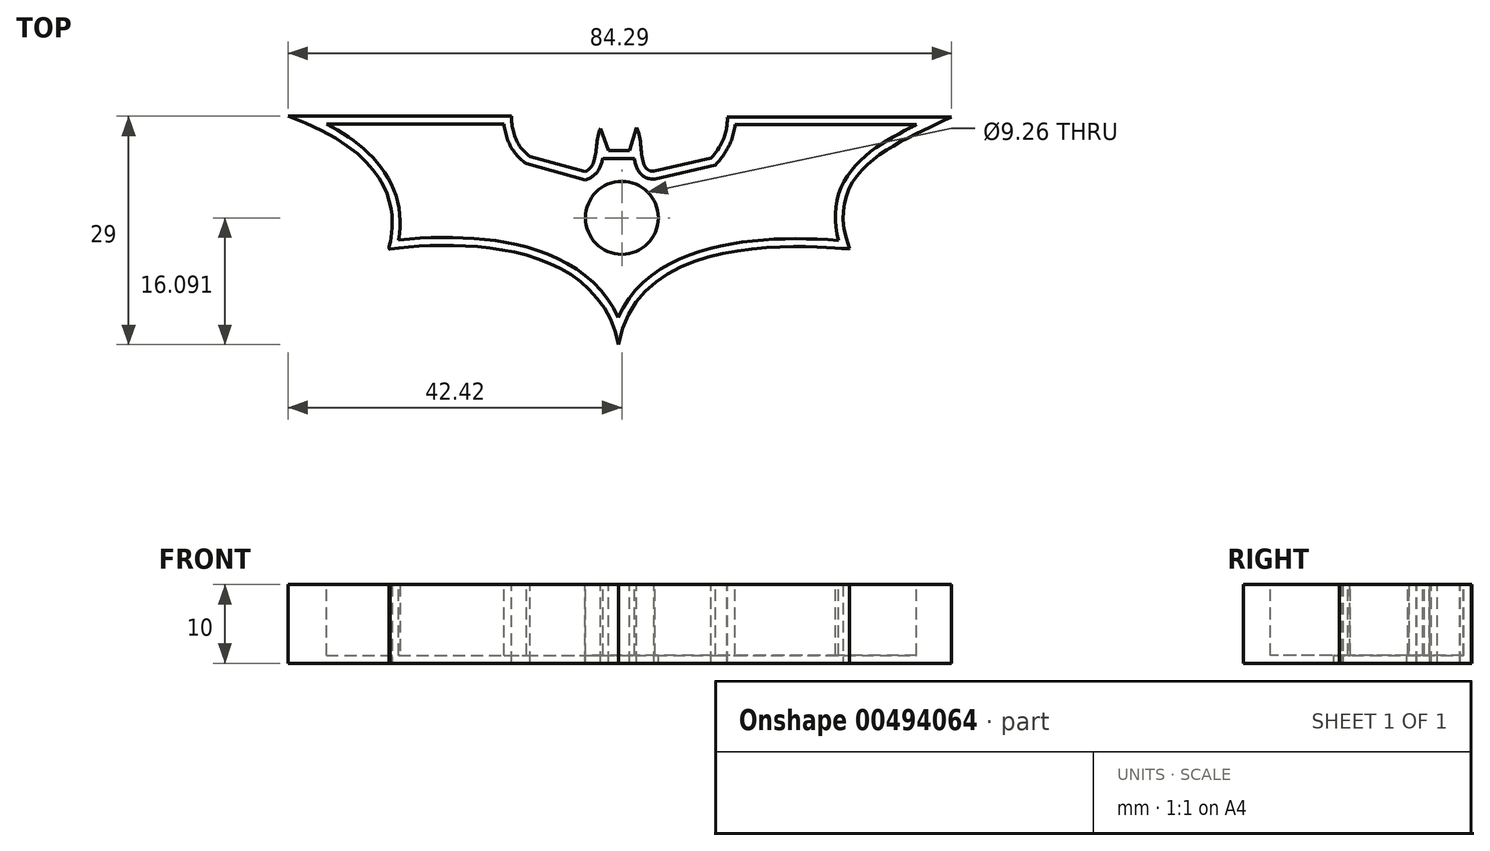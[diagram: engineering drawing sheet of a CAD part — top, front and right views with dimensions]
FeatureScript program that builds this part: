
annotation { "Feature Type Name" : "Feature", "Feature Type Description" : "" }
export const myFeature = defineFeature(function(context is Context, id is Id, definition is map)
    precondition{}
    {
        {
            var Q0;
            Q0=qCreatedBy(makeId("Top.planeOp"),FACE);
            var sketch = newSketch(context, id + "F0", { "sketchPlane" : qUnion([Q0])});
            skLineSegment(sketch, "E0", {"start": v(-42.42, 31.71) * mm, "end": v(-14.02, 31.71) * mm});
            skLineSegment(sketch, "E1", {"start": v(13.38, 31.62) * mm, "end": v(41.87, 31.62) * mm});
            skLineSegment(sketch, "E2", {"start": v(-2.73, 30.17) * mm, "end": v(-1.7, 27.33) * mm});
            skLineSegment(sketch, "E3", {"start": v(-1.7, 27.33) * mm, "end": v(0.98, 27.33) * mm});
            skLineSegment(sketch, "E4", {"start": v(0.98, 27.33) * mm, "end": v(1.89, 30.24) * mm});
            skFitSpline(sketch, "E5", {"points": [v(-42.42, 31.71) * mm, v(-29.54, 14.84) * mm, v(-29.44, 14.84) * mm], "startDerivative": vector(55.49, -19.7) * mm, "endDerivative": vector(1.1, 0.55) * mm});
            skFitSpline(sketch, "E6", {"points": [v(-0.4, 2.71) * mm, v(28.89, 14.87) * mm, v(28.92, 14.89) * mm], "startDerivative": vector(7.93, 48.98) * mm, "endDerivative": vector(0.37, 0.49) * mm});
            skFitSpline(sketch, "E7", {"points": [v(28.92, 14.89) * mm, v(41.87, 31.62) * mm], "startDerivative": vector(-11.3, 30.72) * mm, "endDerivative": vector(19.48, 9.75) * mm});
            skLineSegment(sketch, "E8", {"start": v(-11.69, 26.58) * mm, "end": v(-4.7, 24.66) * mm});
            skLineSegment(sketch, "E9", {"start": v(4.1, 24.72) * mm, "end": v(11.35, 26.39) * mm});
            skFitSpline(sketch, "E10", {"points": [v(-14.02, 31.71) * mm, v(-11.69, 26.58) * mm], "startDerivative": vector(0.03, -5.72) * mm, "endDerivative": vector(5.36, -4.02) * mm});
            skPoint(sketch, "E11.1.internal.snap0", {"position": v(-0.36, 27.33) * mm});
            skFitSpline(sketch, "E12", {"points": [v(-4.7, 24.66) * mm, v(-2.73, 30.17) * mm], "startDerivative": vector(5.67, 2.3) * mm, "endDerivative": vector(2.55, 5.42) * mm});
            skFitSpline(sketch, "E13", {"points": [v(1.89, 30.24) * mm, v(4.1, 24.72) * mm], "startDerivative": vector(2.87, -5.83) * mm, "endDerivative": vector(6.52, 0.32) * mm});
            skFitSpline(sketch, "E14", {"points": [v(11.35, 26.39) * mm, v(13.38, 31.62) * mm], "startDerivative": vector(5.41, 6.2) * mm, "endDerivative": vector(-0.27, 4.04) * mm});
            skFitSpline(sketch, "E15", {"points": [v(-29.44, 14.84) * mm, v(-0.4, 2.71) * mm], "startDerivative": vector(25.03, 3.27) * mm, "endDerivative": vector(8.63, -40.54) * mm});
            skSolve(sketch);
        }
        {
            var Q0;
            Q0 = qSketchRegion(id + "F0", true);
            extrude(context, id + "F1", {"entities" : qUnion([Q0]), "oppositeDirection" : true, "depth" : 10 * mm});
        }
        {
            var Q0;
            Q0=makeQuery(id+"F1.opExtrude","CAP_FACE",FACE,{"disambiguationData":[OSD([sQuery(id+"F0.wireOp",EDGE,"E0"),sQuery(id+"F0.wireOp",EDGE,"E1"),sQuery(id+"F0.wireOp",EDGE,"E2"),sQuery(id+"F0.wireOp",EDGE,"E3"),sQuery(id+"F0.wireOp",EDGE,"E4"),sQuery(id+"F0.wireOp",EDGE,"E5"),sQuery(id+"F0.wireOp",EDGE,"E6"),sQuery(id+"F0.wireOp",EDGE,"E7"),sQuery(id+"F0.wireOp",EDGE,"E8"),sQuery(id+"F0.wireOp",EDGE,"E9"),sQuery(id+"F0.wireOp",EDGE,"E10"),sQuery(id+"F0.wireOp",EDGE,"E12"),sQuery(id+"F0.wireOp",EDGE,"E13"),sQuery(id+"F0.wireOp",EDGE,"E14"),sQuery(id+"F0.wireOp",EDGE,"E15")])],"isStart":true});
            shell(context, id + "F2", {"entities" : qUnion([Q0]), "thickness" : 1 * mm});
        }
        {
            var Q0;
            Q0=makeQuery(id+"F2.opShell","OFFSET_FACE",FACE,{"disambiguationData":[OSD([sQuery(id+"F0.wireOp",EDGE,"E0"),sQuery(id+"F0.wireOp",EDGE,"E1"),sQuery(id+"F0.wireOp",EDGE,"E2"),sQuery(id+"F0.wireOp",EDGE,"E3"),sQuery(id+"F0.wireOp",EDGE,"E4"),sQuery(id+"F0.wireOp",EDGE,"E5"),sQuery(id+"F0.wireOp",EDGE,"E6"),sQuery(id+"F0.wireOp",EDGE,"E7"),sQuery(id+"F0.wireOp",EDGE,"E8"),sQuery(id+"F0.wireOp",EDGE,"E9"),sQuery(id+"F0.wireOp",EDGE,"E10"),sQuery(id+"F0.wireOp",EDGE,"E12"),sQuery(id+"F0.wireOp",EDGE,"E13"),sQuery(id+"F0.wireOp",EDGE,"E14"),sQuery(id+"F0.wireOp",EDGE,"E15")])]});
            var sketch = newSketch(context, id + "F3", { "sketchPlane" : qUnion([Q0])});
            skCircle(sketch, "E16", {"center": v(0, 18.8) * mm, "radius": 4.63 * mm});
            skSolve(sketch);
        }
        {
            var Q0;
            Q0=makeQuery(id+"F3.imprint","IMPRINT",FACE,{"disambiguationData":[TD([[makeQuery(id+"F3.imprint","IMPRINT",EDGE,{"derivedFrom":sQuery(id+"F3.wireOp",EDGE,"E16")}),1.0]])]});
            extrude(context, id + "F4", {"entities" : qUnion([Q0]), "operationType" : NewBodyOperationType.REMOVE, "oppositeDirection" : true, "depth" : 25 * mm});
        }
    });
